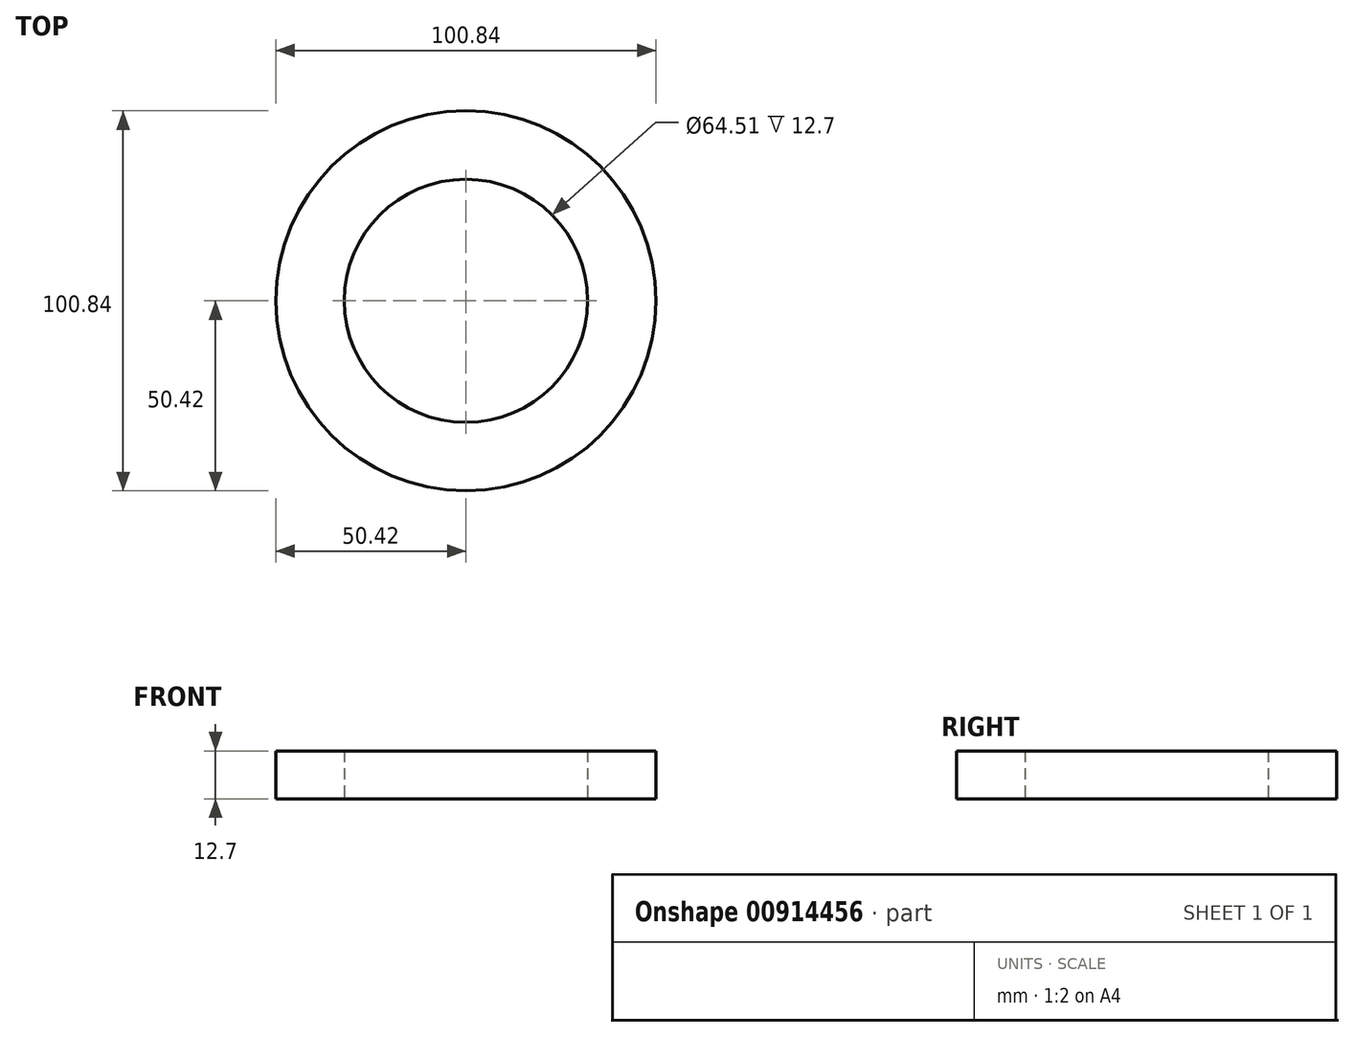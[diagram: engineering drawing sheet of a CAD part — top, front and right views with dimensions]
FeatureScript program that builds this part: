
annotation { "Feature Type Name" : "Feature", "Feature Type Description" : "" }
export const myFeature = defineFeature(function(context is Context, id is Id, definition is map)
    precondition{}
    {
        {
            var Q0;
            Q0=qCreatedBy(makeId("Top.planeOp"),FACE);
            var sketch = newSketch(context, id + "F0", { "sketchPlane" : qUnion([Q0])});
            skCircle(sketch, "E0", {"center": v(0, 0) * mm, "radius": 50.42 * mm});
            skCircle(sketch, "E1", {"center": v(0, 0) * mm, "radius": 32.26 * mm});
            skCircle(sketch, "E2", {"center": v(0, 0) * mm, "radius": 15.9 * mm});
            skSolve(sketch);
        }
        {
            var Q0;
            Q0 = qSketchRegion(id + "F0", true);
            extrude(context, id + "F1", {"entities" : qUnion([Q0]), "depth" : 12.7 * mm, "offsetDistance" : 25.4 * mm});
        }
    });
